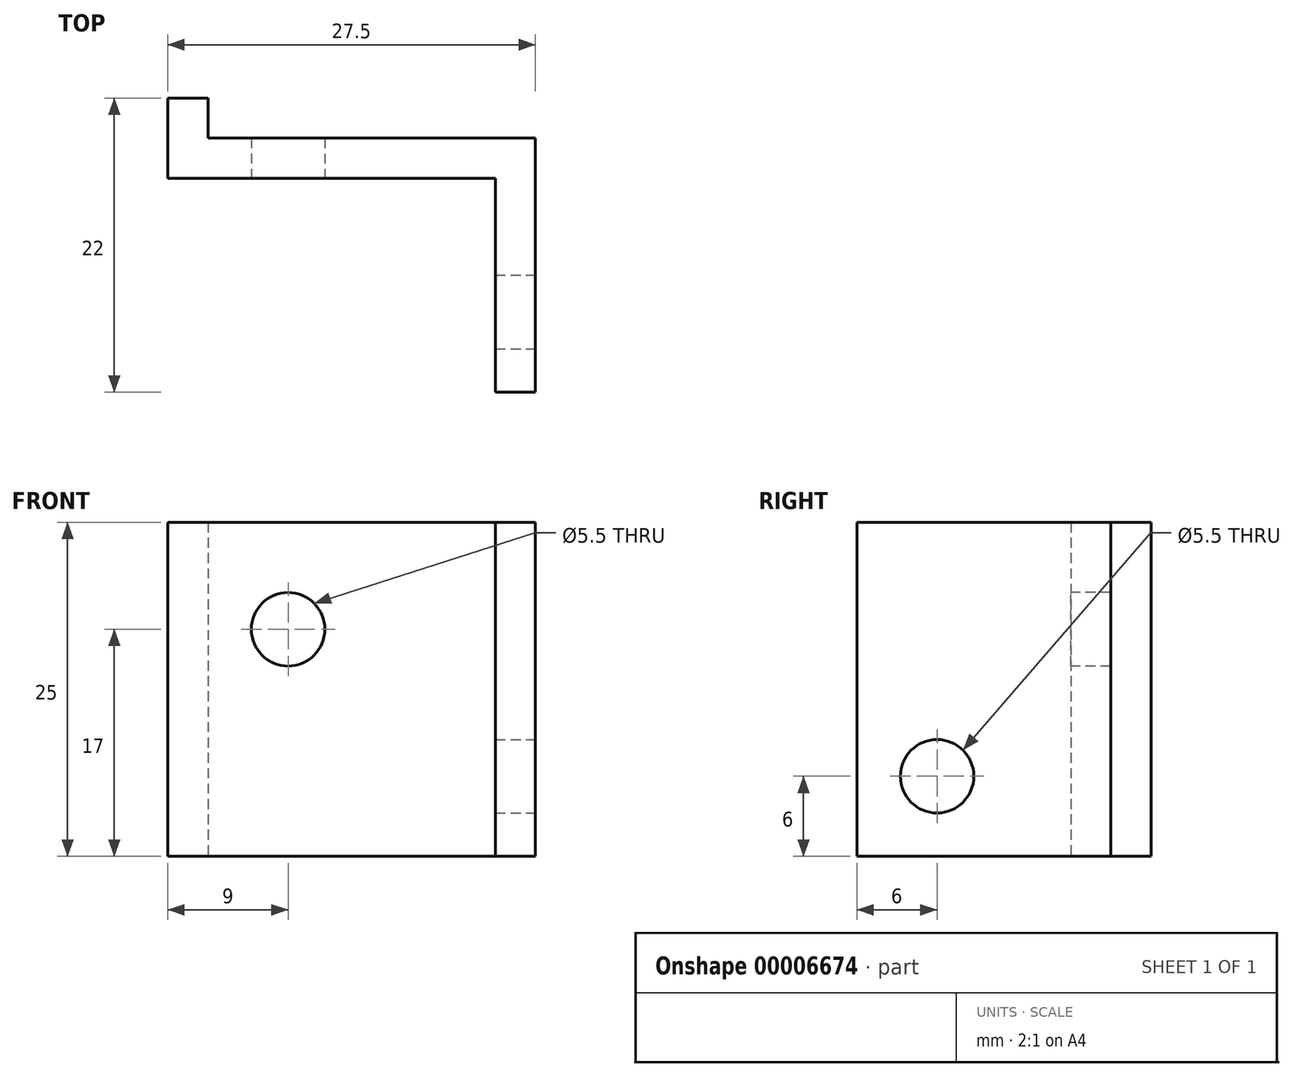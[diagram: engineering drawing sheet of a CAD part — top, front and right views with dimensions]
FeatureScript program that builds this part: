
annotation { "Feature Type Name" : "Feature", "Feature Type Description" : "" }
export const myFeature = defineFeature(function(context is Context, id is Id, definition is map)
    precondition{}
    {
        {
            var Q0;
            Q0=qCreatedBy(makeId("Top.planeOp"),FACE);
            var sketch = newSketch(context, id + "F0", { "sketchPlane" : qUnion([Q0])});
            skLineSegment(sketch, "E0.bottom", {"start": v(3, 0) * mm, "end": v(27.5, 0) * mm});
            skLineSegment(sketch, "E0.top", {"start": v(0, -3) * mm, "end": v(24.5, -3) * mm});
            skLineSegment(sketch, "E0.left", {"start": v(0, 3) * mm, "end": v(0, -3) * mm});
            skLineSegment(sketch, "E1.0", {"start": v(0, 3) * mm, "end": v(3, 3) * mm});
            skLineSegment(sketch, "E2.0", {"start": v(3, 3) * mm, "end": v(3, 0) * mm});
            skLineSegment(sketch, "E3.0", {"start": v(27.5, 0) * mm, "end": v(27.5, -19) * mm});
            skLineSegment(sketch, "E4.0", {"start": v(24.5, -3) * mm, "end": v(24.5, -19) * mm});
            skLineSegment(sketch, "E5.0", {"start": v(24.5, -19) * mm, "end": v(27.5, -19) * mm});
            skSolve(sketch);
        }
        {
            var Q0;
            Q0 = qSketchRegion(id + "F0", true);
            extrude(context, id + "F1", {"entities" : qUnion([Q0]), "depth" : 25 * mm});
        }
        {
            var Q0;
            Q0=makeQuery(id+"F1.opExtrude","SWEPT_FACE",FACE,{"disambiguationData":[OSD([sQuery(id+"F0.wireOp",EDGE,"E0.top")])]});
            var sketch = newSketch(context, id + "F2", { "sketchPlane" : qUnion([Q0])});
            skCircle(sketch, "E6", {"center": v(9, 17) * mm, "radius": 2.75 * mm});
            skSolve(sketch);
        }
        {
            var Q0;
            Q0 = qSketchRegion(id + "F2", true);
            extrude(context, id + "F3", {"entities" : qUnion([Q0]), "operationType" : NewBodyOperationType.REMOVE, "endBound" : BoundingType.THROUGH_ALL, "oppositeDirection" : true, "depth" : 25 * mm});
        }
        {
            var Q0;
            Q0=makeQuery(id+"F1.opExtrude","SWEPT_FACE",FACE,{"disambiguationData":[OSD([sQuery(id+"F0.wireOp",EDGE,"E3.0")])]});
            var sketch = newSketch(context, id + "F4", { "sketchPlane" : qUnion([Q0])});
            skCircle(sketch, "E7", {"center": v(-13, 6) * mm, "radius": 2.75 * mm});
            skSolve(sketch);
        }
        {
            var Q0;
            Q0 = qSketchRegion(id + "F4", true);
            extrude(context, id + "F5", {"entities" : qUnion([Q0]), "operationType" : NewBodyOperationType.REMOVE, "endBound" : BoundingType.THROUGH_ALL, "oppositeDirection" : true, "depth" : 25 * mm});
        }
    });
